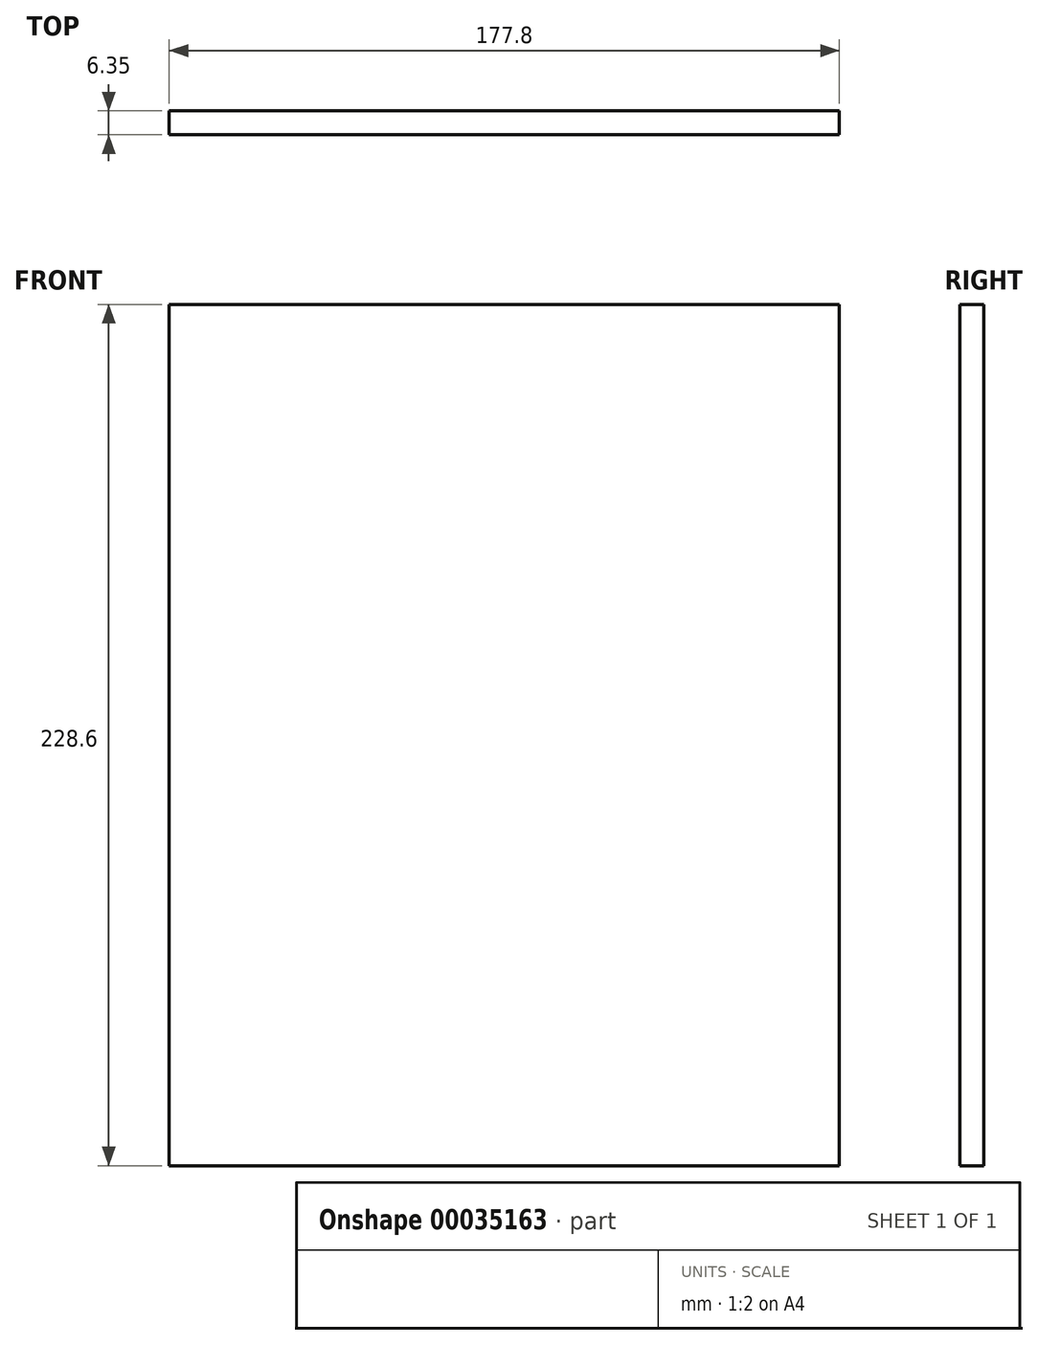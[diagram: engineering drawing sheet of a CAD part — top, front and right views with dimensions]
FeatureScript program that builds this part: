
annotation { "Feature Type Name" : "Feature", "Feature Type Description" : "" }
export const myFeature = defineFeature(function(context is Context, id is Id, definition is map)
    precondition{}
    {
        {
            var Q0;
            Q0=qCreatedBy(makeId("Front.planeOp"),FACE);
            var sketch = newSketch(context, id + "F0", { "sketchPlane" : qUnion([Q0])});
            skLineSegment(sketch, "E0.bottom", {"start": v(-80.6, 110.81) * mm, "end": v(97.2, 110.81) * mm});
            skLineSegment(sketch, "E0.top", {"start": v(-80.6, -117.79) * mm, "end": v(97.2, -117.79) * mm});
            skLineSegment(sketch, "E0.left", {"start": v(-80.6, 110.81) * mm, "end": v(-80.6, -117.79) * mm});
            skLineSegment(sketch, "E0.right", {"start": v(97.2, 110.81) * mm, "end": v(97.2, -117.79) * mm});
            skSolve(sketch);
        }
        {
            var Q0;
            Q0 = qSketchRegion(id + "F0", true);
            extrude(context, id + "F1", {"entities" : qUnion([Q0]), "depth" : 6.35 * mm});
        }
    });
